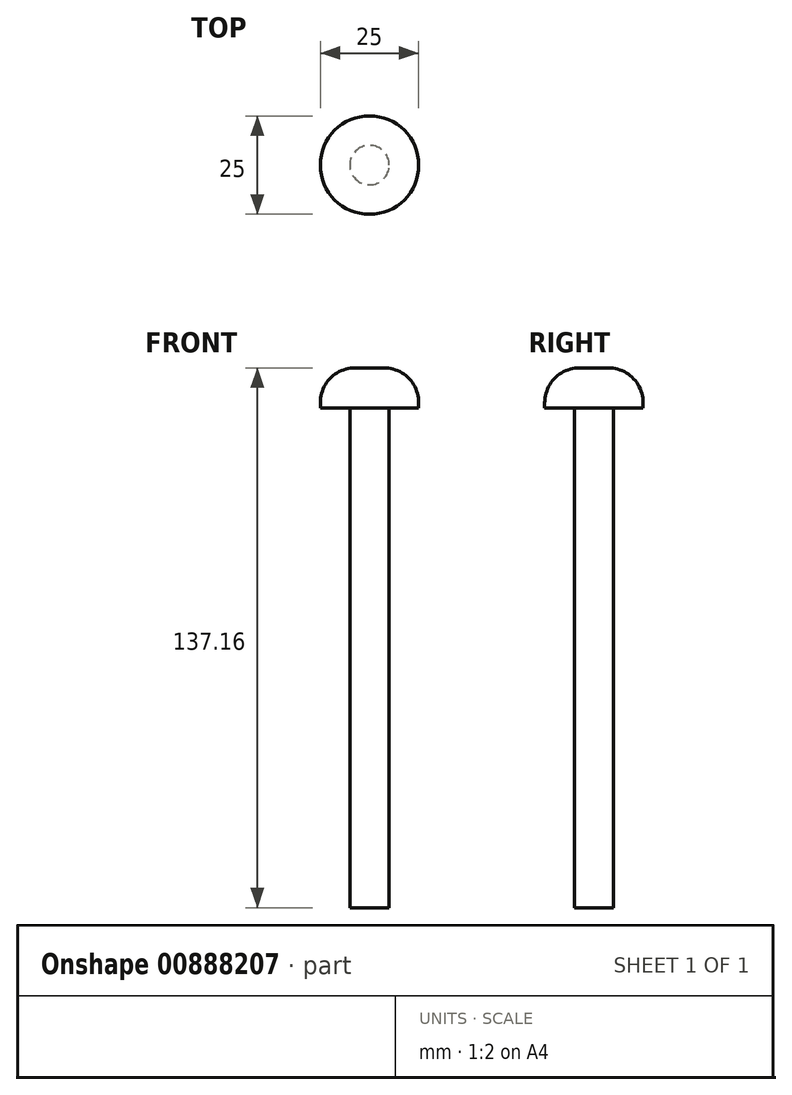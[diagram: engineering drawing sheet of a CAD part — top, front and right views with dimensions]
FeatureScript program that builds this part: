
annotation { "Feature Type Name" : "Feature", "Feature Type Description" : "" }
export const myFeature = defineFeature(function(context is Context, id is Id, definition is map)
    precondition{}
    {
        {
            var Q0;
            Q0=qCreatedBy(makeId("Top.planeOp"),FACE);
            var sketch = newSketch(context, id + "F0", { "sketchPlane" : qUnion([Q0])});
            skCircle(sketch, "E0", {"center": v(0, 0) * mm, "radius": 5 * mm});
            skSolve(sketch);
        }
        {
            var Q0;
            Q0 = qSketchRegion(id + "F0", true);
            extrude(context, id + "F1", {"entities" : qUnion([Q0]), "depth" : 127 * mm, "offsetDistance" : 25.4 * mm});
        }
        {
            var Q0;
            Q0=makeQuery(id+"F1.opExtrude","CAP_FACE",FACE,{"disambiguationData":[OSD([sQuery(id+"F0.wireOp",EDGE,"E0")])],"isStart":false});
            var sketch = newSketch(context, id + "F2", { "sketchPlane" : qUnion([Q0])});
            skCircle(sketch, "E1", {"center": v(0, 0) * mm, "radius": 12.5 * mm});
            skSolve(sketch);
        }
        {
            var Q0;
            Q0=makeQuery(id+"F2.imprint","IMPRINT",FACE,{"disambiguationData":[TD([[makeQuery(id+"F2.imprint","IMPRINT",EDGE,{"derivedFrom":sQuery(id+"F2.wireOp",EDGE,"E1")}),1.0]])]});
            var Q1;
            Q1=makeQuery(id+"F2.imprint","IMPRINT",FACE,{"disambiguationData":[TD([[makeQuery(id+"F2.imprint","IMPRINT",EDGE,{"derivedFrom":makeQuery(id+"F1.opExtrude","CAP_EDGE",EDGE,{"disambiguationData":[OSD([sQuery(id+"F0.wireOp",EDGE,"E0")])],"isStart":false})}),1.0]])]});
            extrude(context, id + "F3", {"entities" : qUnion([Q0, Q1]), "operationType" : NewBodyOperationType.ADD, "depth" : 10.16 * mm, "offsetDistance" : 25.4 * mm});
        }
        {
            var Q0;
            Q0=makeQuery(id+"F3.opExtrude","CAP_EDGE",EDGE,{"disambiguationData":[OSD([sQuery(id+"F2.wireOp",EDGE,"E1")])],"isStart":false});
            fillet(context, id + "F4", {"entities" : qUnion([Q0]), "radius" : 8.9 * mm, "tangentPropagation" : true, "allowEdgeOverflow" : false});
        }
    });
